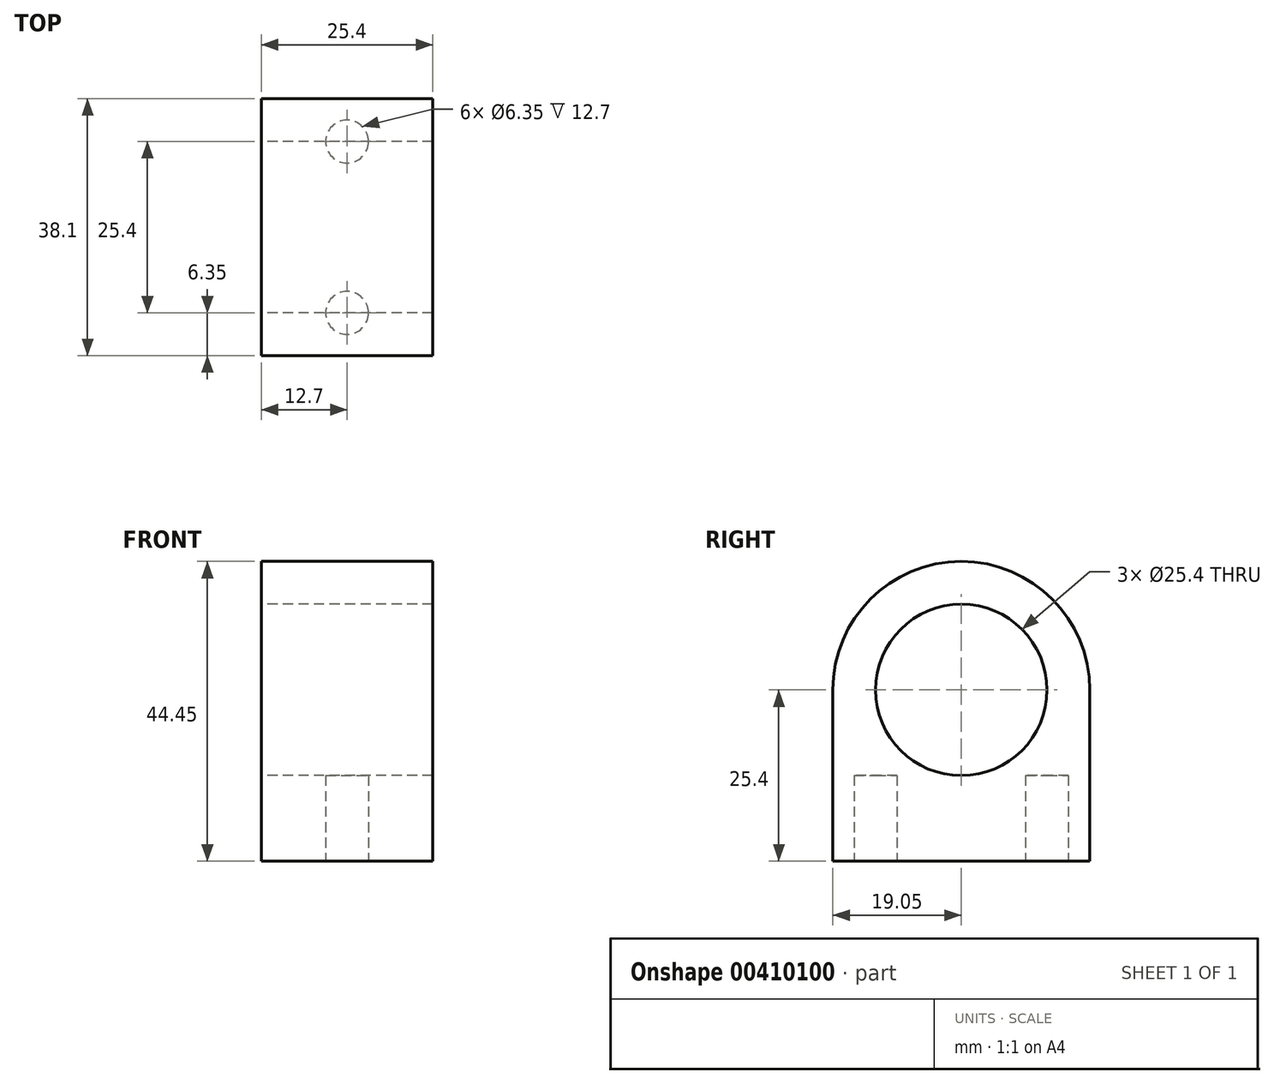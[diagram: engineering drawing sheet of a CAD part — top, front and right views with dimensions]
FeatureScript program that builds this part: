
annotation { "Feature Type Name" : "Feature", "Feature Type Description" : "" }
export const myFeature = defineFeature(function(context is Context, id is Id, definition is map)
    precondition{}
    {
        {
            var Q0;
            Q0=qCreatedBy(makeId("Right.planeOp"),FACE);
            var sketch = newSketch(context, id + "F0", { "sketchPlane" : qUnion([Q0])});
            skArc(sketch, "E0", {"start": v(19.05, 0) * mm, "mid": v(0, 19.05) * mm, "end": v(-19.05, 0) * mm});
            skCircle(sketch, "E1", {"center": v(0, 0) * mm, "radius": 12.7 * mm});
            skLineSegment(sketch, "E2", {"start": v(-19.05, -25.4) * mm, "end": v(19.05, -25.4) * mm});
            skLineSegment(sketch, "E3", {"start": v(19.05, 0) * mm, "end": v(19.05, -25.4) * mm});
            skLineSegment(sketch, "E4", {"start": v(-19.05, 0) * mm, "end": v(-19.05, -25.4) * mm});
            skSolve(sketch);
        }
        {
            var Q0;
            Q0 = qSketchRegion(id + "F0", true);
            extrude(context, id + "F1", {"entities" : qUnion([Q0]), "depth" : 25.4 * mm});
        }
        {
            var Q0;
            Q0=makeQuery(id+"F1.opExtrude","SWEPT_FACE",FACE,{"disambiguationData":[OSD([sQuery(id+"F0.wireOp",EDGE,"E2")])]});
            var sketch = newSketch(context, id + "F2", { "sketchPlane" : qUnion([Q0])});
            skLineSegment(sketch, "E5.0.0", {"start": v(0, 19.05) * mm, "end": v(0, -19.05) * mm});
            skLineSegment(sketch, "E5.0.1", {"start": v(0, -19.05) * mm, "end": v(25.4, -19.05) * mm});
            skLineSegment(sketch, "E5.0.2", {"start": v(25.4, -19.05) * mm, "end": v(25.4, 19.05) * mm});
            skLineSegment(sketch, "E5.0.3", {"start": v(25.4, 19.05) * mm, "end": v(0, 19.05) * mm});
            skCircle(sketch, "E6", {"center": v(12.7, -12.7) * mm, "radius": 3.18 * mm});
            skCircle(sketch, "E7", {"center": v(12.7, 12.7) * mm, "radius": 3.18 * mm});
            skLineSegment(sketch, "E8", {"start": v(0, 0) * mm, "end": v(37.35, 0) * mm});
            skPoint(sketch, "E8.endSnap0", {"position": v(25.4, 0) * mm});
            skSolve(sketch);
        }
        {
            var Q0;
            Q0=makeQuery(id+"F2.imprint","IMPRINT",FACE,{"disambiguationData":[TD([[makeQuery(id+"F2.imprint","IMPRINT",EDGE,{"derivedFrom":sQuery(id+"F2.wireOp",EDGE,"E6")}),1.0]])]});
            var Q1;
            Q1=makeQuery(id+"F2.imprint","IMPRINT",FACE,{"disambiguationData":[TD([[makeQuery(id+"F2.imprint","IMPRINT",EDGE,{"derivedFrom":sQuery(id+"F2.wireOp",EDGE,"E7")}),1.0]])]});
            extrude(context, id + "F3", {"entities" : qUnion([Q0, Q1]), "operationType" : NewBodyOperationType.REMOVE, "oppositeDirection" : true, "depth" : 12.7 * mm});
        }
    });
